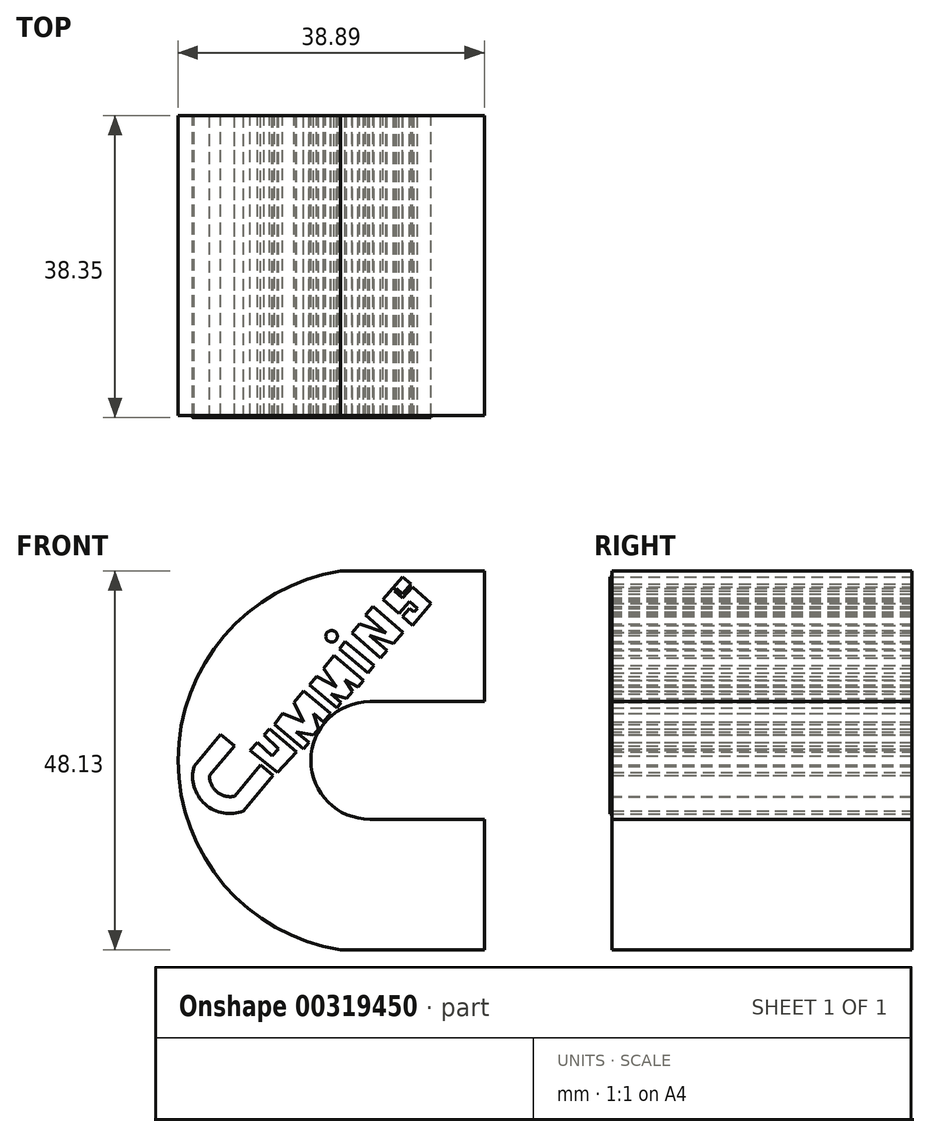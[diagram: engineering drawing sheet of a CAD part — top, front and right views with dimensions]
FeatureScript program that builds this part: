
annotation { "Feature Type Name" : "Feature", "Feature Type Description" : "" }
export const myFeature = defineFeature(function(context is Context, id is Id, definition is map)
    precondition{}
    {
        {
            var Q0;
            Q0=qCreatedBy(makeId("Front.planeOp"),FACE);
            var sketch = newSketch(context, id + "F0", { "sketchPlane" : qUnion([Q0])});
            skLineSegment(sketch, "E0", {"start": v(0, 48.13) * mm, "end": v(-18.26, 48.13) * mm});
            skLineSegment(sketch, "E1", {"start": v(-18.26, 0) * mm, "end": v(0, 0) * mm});
            skLineSegment(sketch, "E2", {"start": v(0, 0) * mm, "end": v(0, 16.59) * mm});
            skLineSegment(sketch, "E3", {"start": v(0, 16.59) * mm, "end": v(-14.53, 16.59) * mm});
            skLineSegment(sketch, "E4", {"start": v(-14.53, 31.54) * mm, "end": v(0, 31.54) * mm});
            skLineSegment(sketch, "E5", {"start": v(0, 31.54) * mm, "end": v(0, 48.13) * mm});
            skArc(sketch, "E6", {"start": v(-18.26, 48.13) * mm, "mid": v(-38.89, 24.06) * mm, "end": v(-18.26, 0) * mm});
            skArc(sketch, "E7", {"start": v(-14.53, 31.54) * mm, "mid": v(-22.01, 24.06) * mm, "end": v(-14.53, 16.59) * mm});
            skPoint(sketch, "E8", {"position": v(-22.01, 24.06) * mm});
            skPoint(sketch, "E9", {"position": v(-38.89, 24.06) * mm});
            skSolve(sketch);
        }
        {
            var Q0;
            Q0=qCreatedBy(makeId("Front.planeOp"),FACE);
            var sketch = newSketch(context, id + "F1", { "sketchPlane" : qUnion([Q0])});
            skLineSegment(sketch, "E10", {"start": v(-36.87, 23.31) * mm, "end": v(-33.5, 27.36) * mm});
            skLineSegment(sketch, "E11", {"start": v(-33.5, 27.36) * mm, "end": v(-31.74, 25.9) * mm});
            skLineSegment(sketch, "E12", {"start": v(-31.74, 25.9) * mm, "end": v(-34.89, 22.13) * mm});
            skLineSegment(sketch, "E13", {"start": v(-31.74, 19.52) * mm, "end": v(-28.43, 23.5) * mm});
            skLineSegment(sketch, "E14", {"start": v(-28.43, 23.5) * mm, "end": v(-26.8, 22.13) * mm});
            skLineSegment(sketch, "E15", {"start": v(-26.8, 22.13) * mm, "end": v(-30.55, 17.63) * mm});
            skArc(sketch, "E16", {"start": v(-36.87, 23.31) * mm, "mid": v(-35.46, 18.52) * mm, "end": v(-30.55, 17.63) * mm});
            skArc(sketch, "E17", {"start": v(-34.89, 22.13) * mm, "mid": v(-33.95, 20.06) * mm, "end": v(-31.74, 19.52) * mm});
            skLineSegment(sketch, "E18", {"start": v(-29.74, 25.36) * mm, "end": v(-28.83, 26.35) * mm});
            skLineSegment(sketch, "E19", {"start": v(-28.83, 26.35) * mm, "end": v(-26.96, 24.63) * mm});
            skLineSegment(sketch, "E20", {"start": v(-26.96, 24.63) * mm, "end": v(-26.11, 25.55) * mm});
            skLineSegment(sketch, "E21", {"start": v(-26.11, 25.55) * mm, "end": v(-28, 27.28) * mm});
            skLineSegment(sketch, "E22", {"start": v(-28, 27.28) * mm, "end": v(-27.28, 28.05) * mm});
            skLineSegment(sketch, "E23", {"start": v(-27.28, 28.05) * mm, "end": v(-23.82, 25.17) * mm});
            skLineSegment(sketch, "E24", {"start": v(-23.82, 25.17) * mm, "end": v(-26.25, 22.52) * mm});
            skLineSegment(sketch, "E25", {"start": v(-26.25, 22.52) * mm, "end": v(-29.74, 25.36) * mm});
            skLineSegment(sketch, "E26", {"start": v(-26.65, 28.63) * mm, "end": v(-22.95, 25.55) * mm});
            skLineSegment(sketch, "E27", {"start": v(-22.95, 25.55) * mm, "end": v(-22.28, 26.35) * mm});
            skLineSegment(sketch, "E28", {"start": v(-22.28, 26.35) * mm, "end": v(-23.88, 27.69) * mm});
            skLineSegment(sketch, "E29", {"start": v(-23.88, 27.69) * mm, "end": v(-21.7, 27.28) * mm});
            skLineSegment(sketch, "E30", {"start": v(-21.7, 27.28) * mm, "end": v(-21.05, 28.05) * mm});
            skLineSegment(sketch, "E31", {"start": v(-21.05, 28.05) * mm, "end": v(-21.7, 30.02) * mm});
            skLineSegment(sketch, "E32", {"start": v(-21.7, 30.02) * mm, "end": v(-20.42, 28.95) * mm});
            skLineSegment(sketch, "E33", {"start": v(-20.42, 28.95) * mm, "end": v(-19.53, 30.02) * mm});
            skLineSegment(sketch, "E34", {"start": v(-19.53, 30.02) * mm, "end": v(-22.95, 32.87) * mm});
            skLineSegment(sketch, "E35", {"start": v(-22.95, 32.87) * mm, "end": v(-24.15, 31.43) * mm});
            skLineSegment(sketch, "E36", {"start": v(-24.15, 31.43) * mm, "end": v(-22.95, 28.95) * mm});
            skLineSegment(sketch, "E37", {"start": v(-22.95, 28.95) * mm, "end": v(-25.64, 30.02) * mm});
            skLineSegment(sketch, "E38", {"start": v(-25.64, 30.02) * mm, "end": v(-26.65, 28.63) * mm});
            skLineSegment(sketch, "E39", {"start": v(-22.17, 33.64) * mm, "end": v(-18.72, 30.76) * mm});
            skLineSegment(sketch, "E40", {"start": v(-18.72, 30.76) * mm, "end": v(-18.17, 31.43) * mm});
            skLineSegment(sketch, "E41", {"start": v(-18.17, 31.43) * mm, "end": v(-19.44, 32.49) * mm});
            skLineSegment(sketch, "E42", {"start": v(-19.44, 32.49) * mm, "end": v(-17.47, 31.96) * mm});
            skPoint(sketch, "E42.endSnap0", {"position": v(-18.8, 31.96) * mm});
            skLineSegment(sketch, "E43", {"start": v(-17.47, 31.96) * mm, "end": v(-16.76, 32.81) * mm});
            skLineSegment(sketch, "E44", {"start": v(-16.76, 32.81) * mm, "end": v(-17.71, 34.28) * mm});
            skLineSegment(sketch, "E45", {"start": v(-17.71, 34.28) * mm, "end": v(-16.04, 33.4) * mm});
            skLineSegment(sketch, "E46", {"start": v(-16.04, 33.4) * mm, "end": v(-15.33, 34.26) * mm});
            skLineSegment(sketch, "E47", {"start": v(-15.33, 34.26) * mm, "end": v(-19.08, 37.38) * mm});
            skLineSegment(sketch, "E48", {"start": v(-19.08, 37.38) * mm, "end": v(-20.42, 35.78) * mm});
            skLineSegment(sketch, "E49", {"start": v(-20.42, 35.78) * mm, "end": v(-18.75, 33.4) * mm});
            skLineSegment(sketch, "E50", {"start": v(-18.75, 33.4) * mm, "end": v(-21.3, 34.76) * mm});
            skLineSegment(sketch, "E51", {"start": v(-21.3, 34.76) * mm, "end": v(-22.17, 33.64) * mm});
            skLineSegment(sketch, "E52", {"start": v(-18.4, 38.2) * mm, "end": v(-14.77, 35.18) * mm});
            skLineSegment(sketch, "E53", {"start": v(-14.77, 35.18) * mm, "end": v(-13.98, 36.12) * mm});
            skLineSegment(sketch, "E54", {"start": v(-13.98, 36.12) * mm, "end": v(-17.66, 39.19) * mm});
            skLineSegment(sketch, "E55", {"start": v(-17.66, 39.19) * mm, "end": v(-18.4, 38.2) * mm});
            skPoint(sketch, "E56.startSnap0", {"position": v(-20.02, 34.08) * mm});
            skCircle(sketch, "E57", {"center": v(-19.4, 39.84) * mm, "radius": 0.74 * mm});
            skLineSegment(sketch, "E58", {"start": v(-16.82, 40.29) * mm, "end": v(-13.17, 37.1) * mm});
            skLineSegment(sketch, "E59", {"start": v(-13.17, 37.1) * mm, "end": v(-12.35, 38.04) * mm});
            skLineSegment(sketch, "E60", {"start": v(-12.35, 38.04) * mm, "end": v(-14.55, 39.97) * mm});
            skLineSegment(sketch, "E61", {"start": v(-14.55, 39.97) * mm, "end": v(-11.52, 38.93) * mm});
            skLineSegment(sketch, "E62", {"start": v(-11.52, 38.93) * mm, "end": v(-10.3, 40.32) * mm});
            skLineSegment(sketch, "E63", {"start": v(-10.3, 40.32) * mm, "end": v(-14.1, 43.65) * mm});
            skLineSegment(sketch, "E64", {"start": v(-14.1, 43.65) * mm, "end": v(-15.07, 42.55) * mm});
            skLineSegment(sketch, "E65", {"start": v(-15.07, 42.55) * mm, "end": v(-12.48, 40.29) * mm});
            skLineSegment(sketch, "E66", {"start": v(-12.48, 40.29) * mm, "end": v(-15.83, 41.43) * mm});
            skLineSegment(sketch, "E67", {"start": v(-15.83, 41.43) * mm, "end": v(-16.82, 40.29) * mm});
            skLineSegment(sketch, "E68", {"start": v(-10.4, 42.34) * mm, "end": v(-9.49, 43.4) * mm});
            skLineSegment(sketch, "E69", {"start": v(-9.49, 43.4) * mm, "end": v(-8.9, 42.9) * mm});
            skLineSegment(sketch, "E70", {"start": v(-8.9, 42.9) * mm, "end": v(-8.48, 43.4) * mm});
            skLineSegment(sketch, "E71", {"start": v(-8.48, 43.4) * mm, "end": v(-9.49, 44.27) * mm});
            skLineSegment(sketch, "E72", {"start": v(-9.49, 44.27) * mm, "end": v(-10.82, 42.73) * mm});
            skLineSegment(sketch, "E73", {"start": v(-10.82, 42.73) * mm, "end": v(-12.86, 44.5) * mm});
            skLineSegment(sketch, "E74", {"start": v(-12.86, 44.5) * mm, "end": v(-10.36, 47.4) * mm});
            skLineSegment(sketch, "E75", {"start": v(-10.4, 42.34) * mm, "end": v(-9.13, 41.24) * mm});
            skLineSegment(sketch, "E76", {"start": v(-9.13, 41.24) * mm, "end": v(-6.77, 43.98) * mm});
            skLineSegment(sketch, "E77", {"start": v(-10.36, 47.4) * mm, "end": v(-9.29, 46.46) * mm});
            skLineSegment(sketch, "E78", {"start": v(-9.29, 46.46) * mm, "end": v(-10.36, 45.22) * mm});
            skLineSegment(sketch, "E79", {"start": v(-10.36, 45.22) * mm, "end": v(-11.14, 45.9) * mm});
            skLineSegment(sketch, "E80", {"start": v(-11.14, 45.9) * mm, "end": v(-11.4, 45.59) * mm});
            skLineSegment(sketch, "E81", {"start": v(-11.4, 45.59) * mm, "end": v(-10.36, 44.69) * mm});
            skLineSegment(sketch, "E82", {"start": v(-10.36, 44.69) * mm, "end": v(-9.14, 46.1) * mm});
            skLineSegment(sketch, "E83", {"start": v(-9.14, 46.1) * mm, "end": v(-6.77, 43.98) * mm});
            skSolve(sketch);
        }
        {
            var Q0;
            Q0 = qSketchRegion(id + "F1", true);
            extrude(context, id + "F2", {"entities" : qUnion([Q0]), "depth" : 38.35 * mm});
        }
        {
            var Q0;
            Q0 = qSketchRegion(id + "F0", true);
            extrude(context, id + "F3", {"entities" : qUnion([Q0]), "depth" : 38.1 * mm});
        }
    });
